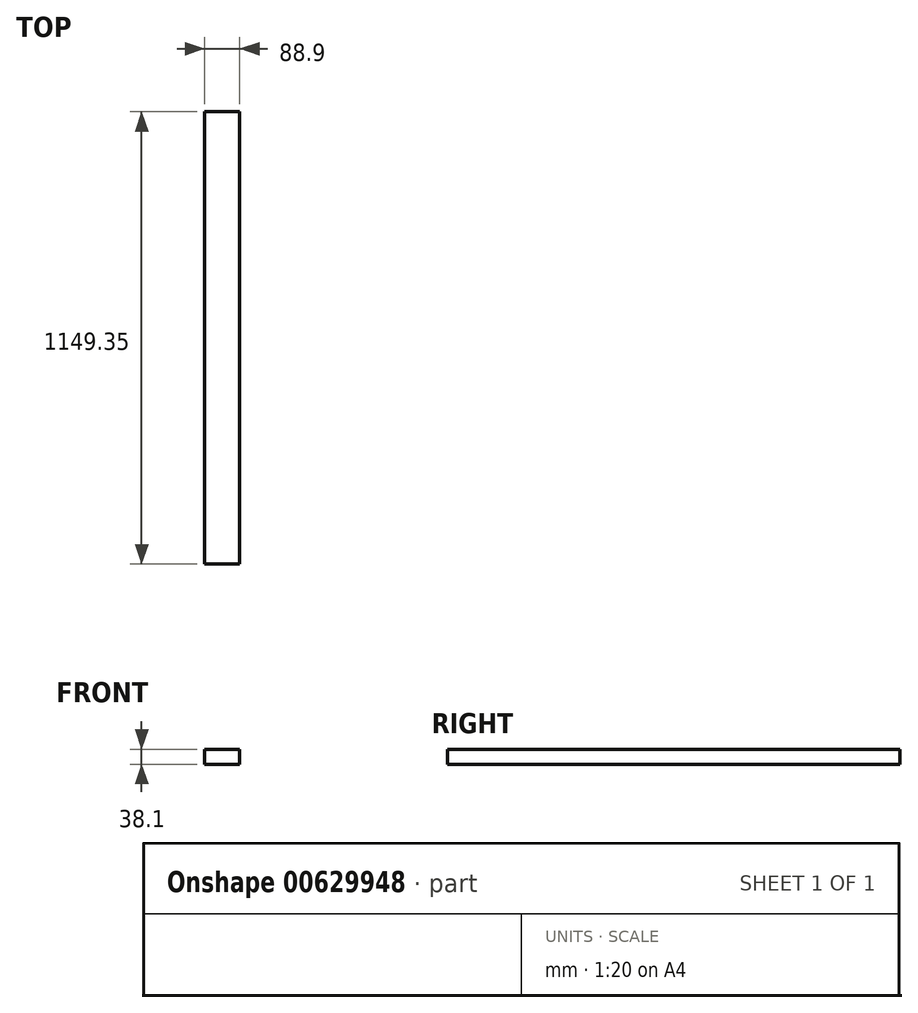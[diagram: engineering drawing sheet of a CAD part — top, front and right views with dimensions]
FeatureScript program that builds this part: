
annotation { "Feature Type Name" : "Feature", "Feature Type Description" : "" }
export const myFeature = defineFeature(function(context is Context, id is Id, definition is map)
    precondition{}
    {
        {
            var Q0;
            Q0=qCreatedBy(makeId("Front.planeOp"),FACE);
            var sketch = newSketch(context, id + "F0", { "sketchPlane" : qUnion([Q0])});
            skLineSegment(sketch, "E0.bottom", {"start": v(-41.2, 38.1) * mm, "end": v(47.7, 38.1) * mm});
            skLineSegment(sketch, "E0.top", {"start": v(-41.2, 0) * mm, "end": v(47.7, 0) * mm});
            skLineSegment(sketch, "E0.left", {"start": v(-41.2, 38.1) * mm, "end": v(-41.2, 0) * mm});
            skLineSegment(sketch, "E0.right", {"start": v(47.7, 38.1) * mm, "end": v(47.7, 0) * mm});
            skSolve(sketch);
        }
        {
            var Q0;
            Q0 = qSketchRegion(id + "F0", true);
            extrude(context, id + "F1", {"entities" : qUnion([Q0]), "depth" : 1149.35 * mm, "offsetDistance" : 25.4 * mm});
        }
    });
